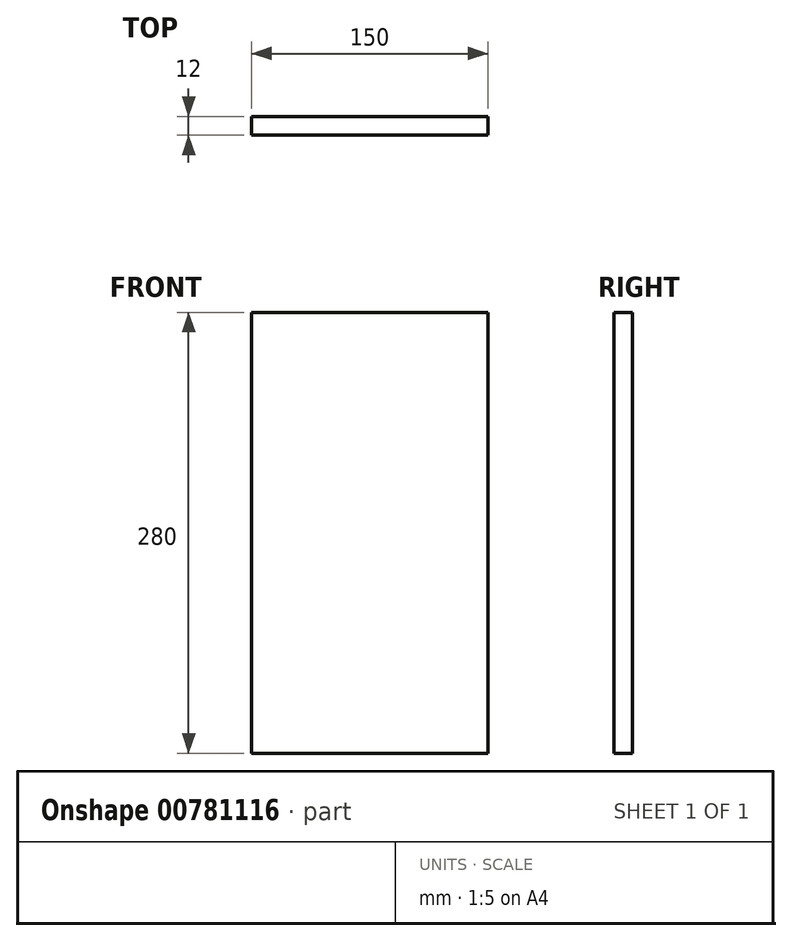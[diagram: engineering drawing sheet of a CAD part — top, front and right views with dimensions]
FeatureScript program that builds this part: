
annotation { "Feature Type Name" : "Feature", "Feature Type Description" : "" }
export const myFeature = defineFeature(function(context is Context, id is Id, definition is map)
    precondition{}
    {
        {
            var Q0;
            Q0=qCreatedBy(makeId("Front.planeOp"),FACE);
            var sketch = newSketch(context, id + "F0", { "sketchPlane" : qUnion([Q0])});
            skLineSegment(sketch, "E0.bottom", {"start": v(-75, 280) * mm, "end": v(75, 280) * mm});
            skLineSegment(sketch, "E0.top", {"start": v(-75, 0) * mm, "end": v(75, 0) * mm});
            skLineSegment(sketch, "E0.left", {"start": v(-75, 280) * mm, "end": v(-75, 0) * mm});
            skLineSegment(sketch, "E0.right", {"start": v(75, 280) * mm, "end": v(75, 0) * mm});
            skSolve(sketch);
        }
        {
            var Q0;
            Q0 = qSketchRegion(id + "F0", true);
            extrude(context, id + "F1", {"entities" : qUnion([Q0]), "depth" : 12 * mm, "offsetDistance" : 25 * mm});
        }
    });
